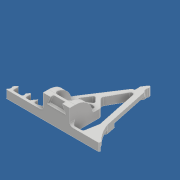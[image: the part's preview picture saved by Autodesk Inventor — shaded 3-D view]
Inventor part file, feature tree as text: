
AUTODESK INVENTOR PART (.ipt)
format: ipt  version: 2017 (Build 210142000, 142)  size: 1,300,480 bytes
history: native  units: mm
features: fillet x26, extrude x20, sketch x20, other x4, mirror x2, chamfer x1
ambient origin geometry x8: Origin, YZ Plane, XZ Plane, XY Plane, X Axis, Y Axis, Z Axis, Center Point
bodies: Body1 (feature_tree)
feature tree (73):
  other  "iPad_mount_left"
  other  "ソリッド1"
  extrude  "押し出し1"  Depth=100.0mm
  extrude  "押し出し2"  Depth=95.0mm
  extrude  "押し出し3"  Depth=20.0mm
  extrude  "押し出し4"  Depth=8.0mm
  other  "作業平面1"
  mirror  "ミラー1"
  extrude  "押し出し6"  Depth=10.0mm
  extrude  "押し出し7"  Depth=8.0mm
  extrude  "押し出し11"  Depth=8.0mm
  extrude  "押し出し14"  Depth=10.0mm TaperAngle=0.0deg
  extrude  "押し出し15"  Depth=40.0mm
  extrude  "押し出し16"  Depth=30.0mm
  extrude  "押し出し17"  Depth=4.0mm
  extrude  "押し出し18"  Depth=20.0mm TaperAngle=0.0deg
  extrude  "押し出し19"  Depth=7.5mm
  extrude  "押し出し20"  Depth=10.0mm
  extrude  "押し出し21"  Depth=15.0mm
  extrude  "押し出し22"  Depth=2.5mm
  extrude  "押し出し23"  Depth=20.0mm TaperAngle=0.0deg
  mirror  "ミラー2"
  extrude  "押し出し24"  Depth=25.0mm
  fillet  "フィレット38"  Radius=3.0mm
  fillet  "フィレット39"  [1 undecoded]
  fillet  "フィレット40"  Radius=10.0mm
  fillet  "フィレット41"  Radius=2.0mm
  fillet  "フィレット42"  Radius=10.0mm
  fillet  "フィレット43"  Radius=10.0mm
  fillet  "フィレット44"  Radius=10.0mm
  fillet  "フィレット45"  Radius=10.0mm
  fillet  "フィレット46"  Radius=2.0mm
  fillet  "フィレット47"  Radius=2.0mm
  fillet  "フィレット48"  Radius=2.0mm
  fillet  "フィレット49"  Radius=3.0mm
  fillet  "フィレット52"  Radius=2.0mm
  fillet  "フィレット53"  Radius=10.0mm
  fillet  "フィレット54"  Radius=5.0mm
  fillet  "フィレット55"  Radius=2.0mm
  fillet  "フィレット56"  Radius=2.0mm
  fillet  "フィレット57"  Radius=2.0mm
  fillet  "フィレット58"  Radius=2.0mm
  fillet  "フィレット59"  Radius=3.0mm
  fillet  "フィレット60"  Radius=7.0mm
  fillet  "フィレット61"  Radius=7.0mm
  fillet  "フィレット63"  Radius=7.0mm
  extrude  "押し出し25"  Depth=6.0mm
  extrude  "押し出し26"  Depth=5.0mm
  chamfer  "面取り1"  Distance=10.0mm
  fillet  "フィレット64"  Radius=9.424778mm
  fillet  "フィレット65"  Radius=30.0mm
  fillet  "フィレット66"  Radius=12.0mm
  sketch  "スケッチ1"
  sketch  "スケッチ2"
  sketch  "スケッチ3"
  sketch  "スケッチ4"
  sketch  "スケッチ7"
  sketch  "スケッチ8"
  sketch  "スケッチ13"
  sketch  "スケッチ17"
  sketch  "スケッチ18"
  sketch  "スケッチ19"
  sketch  "スケッチ20"
  sketch  "スケッチ21"
  sketch  "スケッチ22"
  sketch  "スケッチ23"
  sketch  "スケッチ24"
  sketch  "スケッチ25"
  sketch  "スケッチ26"
  sketch  "スケッチ27"
  sketch  "スケッチ28"
  sketch  "スケッチ29"
  other  "メッシュ フィーチャ2"
note: 1 required parameter value undecoded (feature->parameter linkage not recoverable at this tier; creation-order binding heuristic only, values carry confidence <= 0.55)
